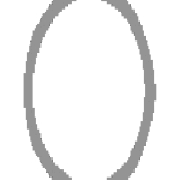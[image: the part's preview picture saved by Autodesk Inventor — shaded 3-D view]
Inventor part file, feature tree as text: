
AUTODESK INVENTOR PART (.ipt)
format: ipt  version: 2021 (Build 250183000, 183)  size: 111,616 bytes
history: native  units: in
note: dims shown in document units (in); Inventor stores cm internally (conversion verified against a paired STEP export)
features: other x4, sketch x3, plane x1
ambient origin geometry x8: Origin, YZ Plane, XZ Plane, XY Plane, X Axis, Y Axis, Z Axis, Center Point
bodies: Solid1 (feature_tree), Body (feature_tree)
feature tree (8):
  other  "Driven Length"
  other  "Frame Generator"
  other  "Start Plane"
  other  "End Plane"
  sketch  "Sketch"  dims[d2=39.5601in d4=-0.0in d5=39.5601in d6=0.12in d7=0.0in d8=90.0deg d9=39.5601in]
  sketch  "Sketch2"  dims[d0=1.0in]
  plane  "Work Plane3"
  sketch  "Sketch3"  dims[d1=0.065in]
